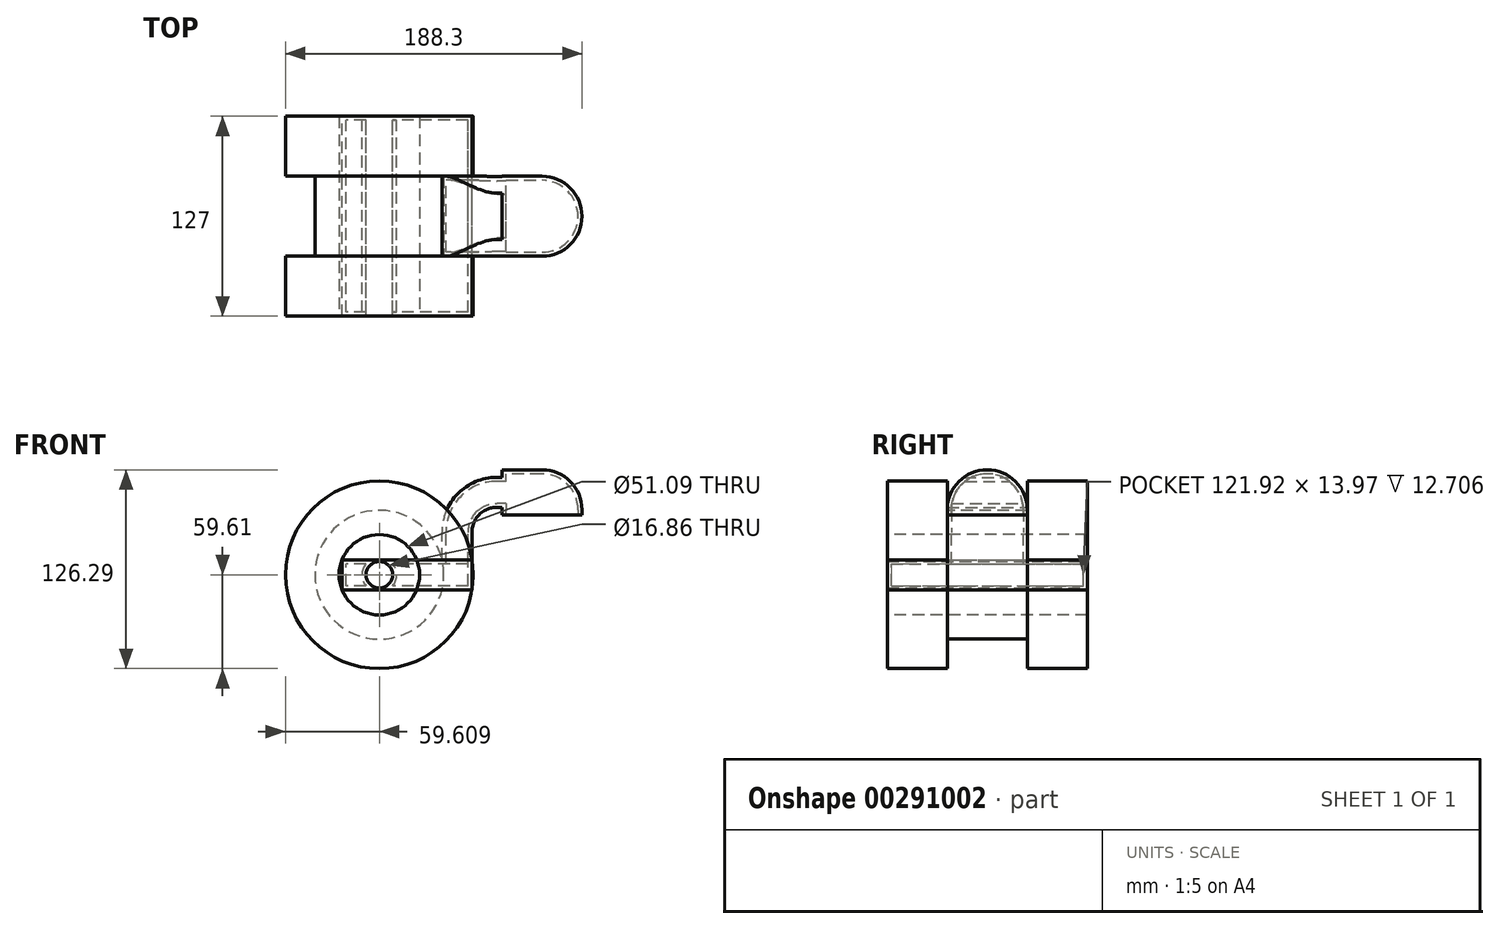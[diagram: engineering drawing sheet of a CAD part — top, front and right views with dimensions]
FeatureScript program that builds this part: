
annotation { "Feature Type Name" : "Feature", "Feature Type Description" : "" }
export const myFeature = defineFeature(function(context is Context, id is Id, definition is map)
    precondition{}
    {
        {
            var Q0;
            Q0=qCreatedBy(makeId("Front.planeOp"),FACE);
            var sketch = newSketch(context, id + "F0", { "sketchPlane" : qUnion([Q0])});
            skLineSegment(sketch, "E0.bottom", {"start": v(41.28, -9.52) * mm, "end": v(-41.27, -9.53) * mm});
            skLineSegment(sketch, "E0.top", {"start": v(41.28, 9.53) * mm, "end": v(-41.28, 9.52) * mm});
            skLineSegment(sketch, "E0.left", {"start": v(41.28, -9.52) * mm, "end": v(41.28, 9.53) * mm});
            skLineSegment(sketch, "E0.right", {"start": v(-41.27, -9.53) * mm, "end": v(-41.27, 9.52) * mm});
            skPoint(sketch, "E0.middle", {"position": v(0, 0) * mm});
            skLineSegment(sketch, "E1.bottom", {"start": v(60.33, 38.1) * mm, "end": v(111.13, 38.1) * mm});
            skLineSegment(sketch, "E1.top", {"start": v(60.33, 66.68) * mm, "end": v(111.13, 66.68) * mm});
            skLineSegment(sketch, "E1.left", {"start": v(60.33, 38.1) * mm, "end": v(60.33, 66.68) * mm});
            skLineSegment(sketch, "E1.right", {"start": v(111.13, 38.1) * mm, "end": v(111.13, 66.68) * mm});
            skPoint(sketch, "E1.middle", {"position": v(85.73, 52.39) * mm});
            skLineSegment(sketch, "E2", {"start": v(41.28, 9.53) * mm, "end": v(41.28, 27) * mm});
            skArc(sketch, "E3", {"start": v(41.28, 27) * mm, "mid": v(45.92, 38.23) * mm, "end": v(57.15, 42.88) * mm});
            skLineSegment(sketch, "E4", {"start": v(57.15, 42.88) * mm, "end": v(85.73, 42.88) * mm});
            skLineSegment(sketch, "E5.0", {"start": v(57.15, 61.93) * mm, "end": v(85.73, 61.93) * mm});
            skArc(sketch, "E5.1", {"start": v(22.23, 27) * mm, "mid": v(32.45, 51.7) * mm, "end": v(57.15, 61.93) * mm});
            skLineSegment(sketch, "E5.2", {"start": v(22.23, 9.53) * mm, "end": v(22.23, 27) * mm});
            skLineSegment(sketch, "E6", {"start": v(85.73, 38.1) * mm, "end": v(85.73, 66.68) * mm});
            skFitSpline(sketch, "E7", {"points": [v(-41.28, 9.52) * mm, v(57.15, 61.93) * mm], "startDerivative": vector(14.23, 138.4) * mm, "endDerivative": vector(235.24, 0.42) * mm});
            skCircle(sketch, "E8", {"center": v(-17.57, 0) * mm, "radius": 8.43 * mm});
            skSolve(sketch);
        }
        {
            var Q0;
            Q0=makeQuery(id+"F0.imprint","IMPRINT",FACE,{"disambiguationData":[TD([[makeQuery(id+"F0.imprint","IMPRINT",EDGE,{"derivedFrom":sQuery(id+"F0.wireOp",EDGE,"E0.bottom")}),-1.0]])]});
            extrude(context, id + "F1", {"entities" : qUnion([Q0]), "endBound" : BoundingType.SYMMETRIC, "depth" : 127 * mm});
        }
        {
            var Q0;
            {var subQ1=sQuery(id+"F0.wireOp",EDGE,"E2");Q0=makeQuery(id+"F0.imprint","IMPRINT",FACE,{"disambiguationData":[TD([[makeQuery(id+"F0.imprint","IMPRINT",EDGE,{"derivedFrom":subQ1}),1.0]])]});}
            var Q1;
            {var subQ0=sQuery(id+"F0.wireOp",EDGE,"E4");var subQ1=sQuery(id+"F0.wireOp",EDGE,"E1.left");var subQ2=makeQuery(id+"F0.imprint","INTERSECT",VERTEX,{"derivedFrom":[subQ1,subQ0]});Q1=makeQuery(id+"F0.imprint","IMPRINT",FACE,{"disambiguationData":[TD([[makeQuery(id+"F0.imprint","IMPRINT",EDGE,{"disambiguationData":[TD([[subQ2,-1.0]])],"derivedFrom":subQ1}),-1.0]])]});}
            extrude(context, id + "F2", {"entities" : qUnion([Q0, Q1]), "operationType" : NewBodyOperationType.ADD, "endBound" : BoundingType.SYMMETRIC, "depth" : 50.8 * mm});
        }
        {
            var Q0;
            {var subQ0=sQuery(id+"F0.wireOp",EDGE,"E1.right");Q0=makeQuery(id+"F0.imprint","IMPRINT",FACE,{"disambiguationData":[TD([[makeQuery(id+"F0.imprint","IMPRINT",EDGE,{"derivedFrom":subQ0}),1.0]])]});}
            var Q1;
            Q1=sQuery(id+"F0.wireOp",EDGE,"E6");
            revolve(context, id + "F3", {"operationType" : NewBodyOperationType.ADD, "entities" : qUnion([Q0]), "axis" : qUnion([Q1]), "revolveType" : RevolveType.FULL});
        }
        {
            var Q0;
            {var subQ0=sQuery(id+"F0.wireOp",EDGE,"E1.left");var subQ1=sQuery(id+"F0.wireOp",EDGE,"E1.top");var subQ2=makeQuery(id+"F0.imprint","INTERSECT",VERTEX,{"derivedFrom":[subQ1,subQ0]});Q0=makeQuery(id+"F0.imprint","IMPRINT",FACE,{"disambiguationData":[TD([[makeQuery(id+"F0.imprint","IMPRINT",EDGE,{"disambiguationData":[TD([[subQ2,-1.0]])],"derivedFrom":subQ1}),-1.0]])]});}
            var Q1;
            {var subQ0=sQuery(id+"F0.wireOp",EDGE,"E1.left");var subQ1=sQuery(id+"F0.wireOp",EDGE,"E1.bottom");var subQ2=makeQuery(id+"F0.imprint","INTERSECT",VERTEX,{"derivedFrom":[subQ1,subQ0]});Q1=makeQuery(id+"F0.imprint","IMPRINT",FACE,{"disambiguationData":[TD([[makeQuery(id+"F0.imprint","IMPRINT",EDGE,{"disambiguationData":[TD([[subQ2,-1.0]])],"derivedFrom":subQ1}),1.0]])]});}
            extrude(context, id + "F4", {"entities" : qUnion([Q0, Q1]), "operationType" : NewBodyOperationType.ADD, "depth" : 25.4 * mm});
        }
        {
            var Q0;
            {var subQ0=sQuery(id+"F0.wireOp",EDGE,"E1.left");var subQ1=sQuery(id+"F0.wireOp",EDGE,"E1.bottom");var subQ2=makeQuery(id+"F0.imprint","INTERSECT",VERTEX,{"derivedFrom":[subQ1,subQ0]});Q0=makeQuery(id+"F0.imprint","IMPRINT",FACE,{"disambiguationData":[TD([[makeQuery(id+"F0.imprint","IMPRINT",EDGE,{"disambiguationData":[TD([[subQ2,-1.0]])],"derivedFrom":subQ1}),1.0]])]});}
            var Q1;
            {var subQ0=sQuery(id+"F0.wireOp",EDGE,"E1.left");var subQ1=sQuery(id+"F0.wireOp",EDGE,"E1.top");var subQ2=makeQuery(id+"F0.imprint","INTERSECT",VERTEX,{"derivedFrom":[subQ1,subQ0]});Q1=makeQuery(id+"F0.imprint","IMPRINT",FACE,{"disambiguationData":[TD([[makeQuery(id+"F0.imprint","IMPRINT",EDGE,{"disambiguationData":[TD([[subQ2,-1.0]])],"derivedFrom":subQ1}),-1.0]])]});}
            extrude(context, id + "F5", {"entities" : qUnion([Q0, Q1]), "operationType" : NewBodyOperationType.ADD, "oppositeDirection" : true, "depth" : 25.4 * mm});
        }
        {
            var Q0;
            Q0=makeQuery(id+"F3.opRevolve","SWEPT_EDGE",EDGE,{"disambiguationData":[OSD([sQuery(id+"F0.wireOp",EDGE,"E1.top"),sQuery(id+"F0.wireOp",EDGE,"E1.right")])]});
            fillet(context, id + "F6", {"entities" : qUnion([Q0]), "radius" : 25.4 * mm, "tangentPropagation" : true, "allowEdgeOverflow" : false});
        }
        {
            var Q0;
            {var subQ0=sQuery(id+"F0.wireOp",EDGE,"E1.bottom");Q0=makeQuery(id+"F5.boolean.opBoolean","MERGE",FACE,{"derivedFrom":[makeQuery(id+"F4.boolean.opBoolean","MERGE",FACE,{"derivedFrom":[makeQuery(id+"F3.opRevolve","SWEPT_FACE",FACE,{"disambiguationData":[OSD([subQ0])]}),makeQuery(id+"F4.opExtrude","SWEPT_FACE",FACE,{"disambiguationData":[OSD([subQ0])]})]}),makeQuery(id+"F5.opExtrude","SWEPT_FACE",FACE,{"disambiguationData":[OSD([subQ0])]})]});}
            shell(context, id + "F7", {"entities" : qUnion([Q0]), "thickness" : 2.54 * mm});
        }
        {
            var Q0;
            Q0=makeQuery(id+"F1.opExtrude","SWEPT_FACE",FACE,{"disambiguationData":[OSD([sQuery(id+"F0.wireOp",EDGE,"E0.top")])]});
            var Q1;
            Q1=sQuery(id+"F0.wireOp",EDGE,"E8");
            sweep(context, id + "F8", {"profiles" : qUnion([Q0]), "path" : qUnion([Q1])});
        }
    });
